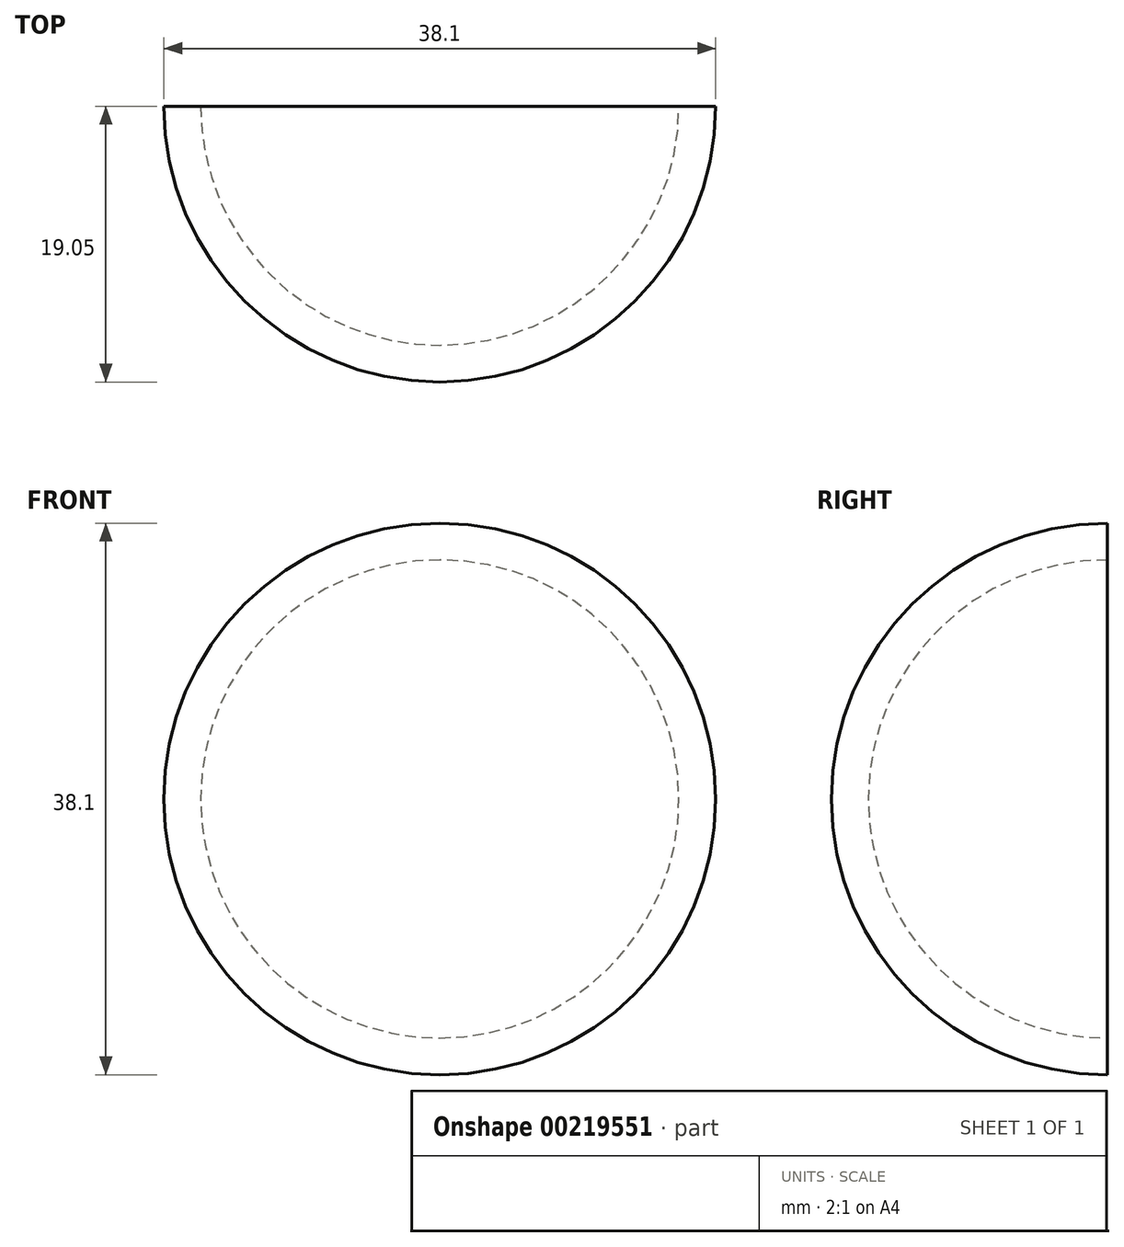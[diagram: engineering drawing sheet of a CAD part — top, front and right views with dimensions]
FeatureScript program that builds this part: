
annotation { "Feature Type Name" : "Feature", "Feature Type Description" : "" }
export const myFeature = defineFeature(function(context is Context, id is Id, definition is map)
    precondition{}
    {
        {
            var Q0;
            Q0=qCreatedBy(makeId("Front.planeOp"),FACE);
            var sketch = newSketch(context, id + "F0", { "sketchPlane" : qUnion([Q0])});
            skArc(sketch, "E0", {"start": v(0, 19.05) * mm, "mid": v(-19.05, 0) * mm, "end": v(0, -19.05) * mm});
            skLineSegment(sketch, "E1", {"start": v(0, 19.05) * mm, "end": v(0, 16.51) * mm});
            skLineSegment(sketch, "E2", {"start": v(0, -16.51) * mm, "end": v(0, -19.05) * mm});
            skArc(sketch, "E3", {"start": v(0, 16.51) * mm, "mid": v(-16.51, 0) * mm, "end": v(0, -16.51) * mm});
            skSolve(sketch);
        }
        {
            var Q0;
            Q0=makeQuery(id+"F0.imprint","IMPRINT",FACE,{"disambiguationData":[TD([[makeQuery(id+"F0.imprint","IMPRINT",EDGE,{"derivedFrom":sQuery(id+"F0.wireOp",EDGE,"E0")}),1.0]])]});
            var Q1;
            Q1=sQuery(id+"F0.wireOp",EDGE,"E1");
            revolve(context, id + "F1", {"entities" : qUnion([Q0]), "axis" : qUnion([Q1]), "revolveType" : RevolveType.ONE_DIRECTION, "oppositeDirection" : true, "angle" : 180 * degree});
        }
    });
